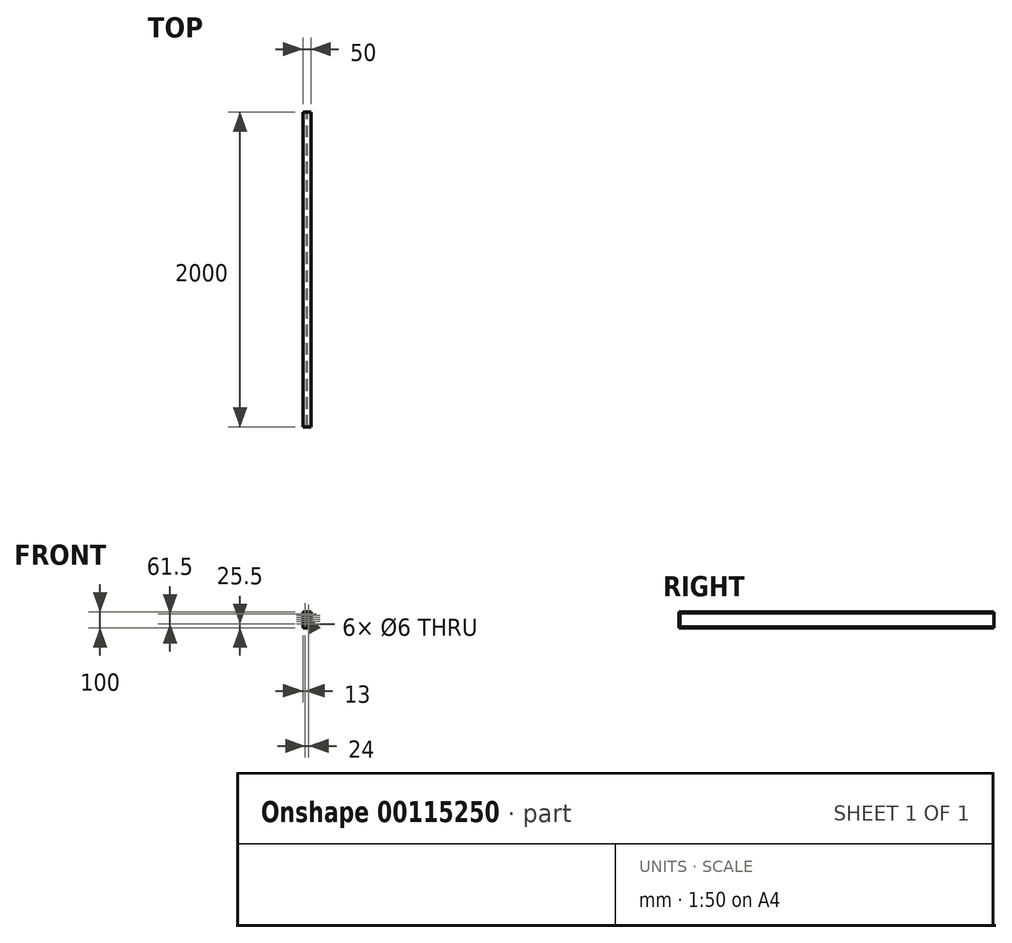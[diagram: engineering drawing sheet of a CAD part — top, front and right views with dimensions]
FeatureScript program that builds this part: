
annotation { "Feature Type Name" : "Feature", "Feature Type Description" : "" }
export const myFeature = defineFeature(function(context is Context, id is Id, definition is map)
    precondition{}
    {
        {
            var Q0;
            Q0=qCreatedBy(makeId("Front.planeOp"),FACE);
            var sketch = newSketch(context, id + "F0", { "sketchPlane" : qUnion([Q0])});
            skLineSegment(sketch, "E0.bottom", {"start": v(25, 50) * mm, "end": v(-25, 50) * mm});
            skLineSegment(sketch, "E0.top", {"start": v(25, -50) * mm, "end": v(-25, -50) * mm});
            skLineSegment(sketch, "E0.left", {"start": v(25, 50) * mm, "end": v(25, 44) * mm});
            skLineSegment(sketch, "E0.right", {"start": v(-25, 50) * mm, "end": v(-25, 44) * mm});
            skLineSegment(sketch, "E1.bottom", {"start": v(-25, 44) * mm, "end": v(-2.5, 44) * mm});
            skLineSegment(sketch, "E1.top", {"start": v(-25, -44) * mm, "end": v(-2.5, -44) * mm});
            skLineSegment(sketch, "E1.right", {"start": v(-2.5, 44) * mm, "end": v(-2.5, -44) * mm});
            skLineSegment(sketch, "E2.bottom", {"start": v(25, 44) * mm, "end": v(2.5, 44) * mm});
            skLineSegment(sketch, "E2.top", {"start": v(25, -44) * mm, "end": v(2.5, -44) * mm});
            skLineSegment(sketch, "E2.right", {"start": v(2.5, 44) * mm, "end": v(2.5, -44) * mm});
            skPoint(sketch, "E3.orphan", {"position": v(0, 50) * mm});
            skPoint(sketch, "E4.orphan", {"position": v(0, -50) * mm});
            skLineSegment(sketch, "E5.trimOffspring", {"start": v(-25, -44) * mm, "end": v(-25, -50) * mm});
            skLineSegment(sketch, "E6.trimOffspring", {"start": v(25, -44) * mm, "end": v(25, -50) * mm});
            skLineSegment(sketch, "E7", {"start": v(0, 50) * mm, "end": v(0, -50) * mm, "construction": true});
            skSolve(sketch);
        }
        {
            var Q0;
            Q0=makeQuery(id+"F0.imprint","IMPRINT",FACE,{"disambiguationData":[TD([[makeQuery(id+"F0.imprint","IMPRINT",EDGE,{"derivedFrom":sQuery(id+"F0.wireOp",EDGE,"E0.bottom")}),1.0]])]});
            extrude(context, id + "F1", {"entities" : qUnion([Q0]), "depth" : 2000 * mm});
        }
        {
            var Q0;
            Q0=makeQuery(id+"F1.opExtrude","CAP_FACE",FACE,{"disambiguationData":[OSD([sQuery(id+"F0.wireOp",EDGE,"E0.bottom"),sQuery(id+"F0.wireOp",EDGE,"E0.top"),sQuery(id+"F0.wireOp",EDGE,"E0.left"),sQuery(id+"F0.wireOp",EDGE,"E0.right"),sQuery(id+"F0.wireOp",EDGE,"E1.bottom"),sQuery(id+"F0.wireOp",EDGE,"E1.top"),sQuery(id+"F0.wireOp",EDGE,"E1.right"),sQuery(id+"F0.wireOp",EDGE,"E2.bottom"),sQuery(id+"F0.wireOp",EDGE,"E2.top"),sQuery(id+"F0.wireOp",EDGE,"E2.right"),sQuery(id+"F0.wireOp",EDGE,"E5.trimOffspring"),sQuery(id+"F0.wireOp",EDGE,"E6.trimOffspring")])],"isStart":false});
            var sketch = newSketch(context, id + "F2", { "sketchPlane" : qUnion([Q0])});
            skLineSegment(sketch, "E8.bottom", {"start": v(-2.5, 44) * mm, "end": v(-25, 44) * mm});
            skLineSegment(sketch, "E8.top", {"start": v(-2.5, -44) * mm, "end": v(-25, -44) * mm});
            skLineSegment(sketch, "E8.left", {"start": v(-2.5, 44) * mm, "end": v(-2.5, -44) * mm});
            skLineSegment(sketch, "E8.right", {"start": v(-25, 44) * mm, "end": v(-25, -44) * mm});
            skSolve(sketch);
        }
        {
            var Q0;
            Q0=makeQuery(id+"F2.imprint","IMPRINT",FACE,{"disambiguationData":[TD([[makeQuery(id+"F2.imprint","IMPRINT",EDGE,{"derivedFrom":sQuery(id+"F2.wireOp",EDGE,"E8.bottom")}),-1.0]])]});
            extrude(context, id + "F3", {"entities" : qUnion([Q0]), "oppositeDirection" : true, "depth" : 6 * mm});
        }
        {
            var Q0;
            Q0=makeQuery(id+"F1.opExtrude","CAP_FACE",FACE,{"disambiguationData":[OSD([sQuery(id+"F0.wireOp",EDGE,"E0.bottom"),sQuery(id+"F0.wireOp",EDGE,"E0.top"),sQuery(id+"F0.wireOp",EDGE,"E0.left"),sQuery(id+"F0.wireOp",EDGE,"E0.right"),sQuery(id+"F0.wireOp",EDGE,"E1.bottom"),sQuery(id+"F0.wireOp",EDGE,"E1.top"),sQuery(id+"F0.wireOp",EDGE,"E1.right"),sQuery(id+"F0.wireOp",EDGE,"E2.bottom"),sQuery(id+"F0.wireOp",EDGE,"E2.top"),sQuery(id+"F0.wireOp",EDGE,"E2.right"),sQuery(id+"F0.wireOp",EDGE,"E5.trimOffspring"),sQuery(id+"F0.wireOp",EDGE,"E6.trimOffspring")])],"isStart":false});
            var sketch = newSketch(context, id + "F4", { "sketchPlane" : qUnion([Q0])});
            skLineSegment(sketch, "E9.bottom", {"start": v(2.5, 44) * mm, "end": v(25, 44) * mm});
            skLineSegment(sketch, "E9.top", {"start": v(2.5, -44) * mm, "end": v(25, -44) * mm});
            skLineSegment(sketch, "E9.left", {"start": v(2.5, 44) * mm, "end": v(2.5, -44) * mm});
            skLineSegment(sketch, "E9.right", {"start": v(25, 44) * mm, "end": v(25, -44) * mm});
            skSolve(sketch);
        }
        {
            var Q0;
            Q0=makeQuery(id+"F4.imprint","IMPRINT",FACE,{"disambiguationData":[TD([[makeQuery(id+"F4.imprint","IMPRINT",EDGE,{"derivedFrom":sQuery(id+"F4.wireOp",EDGE,"E9.bottom")}),1.0]])]});
            extrude(context, id + "F5", {"entities" : qUnion([Q0]), "oppositeDirection" : true, "depth" : 6 * mm});
        }
        {
            var Q0;
            Q0=makeQuery(id+"F5.opExtrude","CAP_FACE",FACE,{"disambiguationData":[OSD([sQuery(id+"F4.wireOp",EDGE,"E9.bottom"),sQuery(id+"F4.wireOp",EDGE,"E9.top"),sQuery(id+"F4.wireOp",EDGE,"E9.left"),sQuery(id+"F4.wireOp",EDGE,"E9.right")])],"isStart":false});
            var sketch = newSketch(context, id + "F6", { "sketchPlane" : qUnion([Q0])});
            skPoint(sketch, "E10", {"position": v(-12, 27.5) * mm});
            skPoint(sketch, "E11", {"position": v(-12, 14.5) * mm});
            skPoint(sketch, "E12", {"position": v(-12, 1.5) * mm});
            skPoint(sketch, "E13", {"position": v(-12, -11.5) * mm});
            skPoint(sketch, "E14", {"position": v(-12, -24.5) * mm});
            skSolve(sketch);
        }
        {
            var Q0;
            Q0=sQuery(id+"F6.wireOp",VERTEX,"E10");
            var Q1;
            Q1=sQuery(id+"F6.wireOp",VERTEX,"E11");
            var Q2;
            Q2=sQuery(id+"F6.wireOp",VERTEX,"E12");
            var Q3;
            Q3=sQuery(id+"F6.wireOp",VERTEX,"E13");
            var Q4;
            Q4=sQuery(id+"F6.wireOp",VERTEX,"E14");
            var Q5;
            Q5=makeQuery(id+"F5.opExtrude","SWEPT_BODY",BODY,{"disambiguationData":[OSD([sQuery(id+"F4.wireOp",EDGE,"E9.bottom"),sQuery(id+"F4.wireOp",EDGE,"E9.top"),sQuery(id+"F4.wireOp",EDGE,"E9.left"),sQuery(id+"F4.wireOp",EDGE,"E9.right")])]});
            hole(context, id + "F7", {"style" : HoleStyle.SIMPLE, "endStyle" : HoleEndStyle.THROUGH, "holeDiameter" : 6 * mm, "locations" : qUnion([Q0, Q1, Q2, Q3, Q4]), "scope" : qUnion([Q5]), "isTappedThrough" : true});
        }
        {
            var Q0;
            Q0=makeQuery(id+"F3.opExtrude","CAP_FACE",FACE,{"disambiguationData":[OSD([sQuery(id+"F2.wireOp",EDGE,"E8.bottom"),sQuery(id+"F2.wireOp",EDGE,"E8.top"),sQuery(id+"F2.wireOp",EDGE,"E8.left"),sQuery(id+"F2.wireOp",EDGE,"E8.right")])],"isStart":false});
            var sketch = newSketch(context, id + "F8", { "sketchPlane" : qUnion([Q0])});
            skPoint(sketch, "E15", {"position": v(12, 37) * mm});
            skSolve(sketch);
        }
        {
            var Q0;
            Q0=sQuery(id+"F8.wireOp",VERTEX,"E15");
            var Q1;
            Q1=makeQuery(id+"F3.opExtrude","SWEPT_BODY",BODY,{"disambiguationData":[OSD([sQuery(id+"F2.wireOp",EDGE,"E8.bottom"),sQuery(id+"F2.wireOp",EDGE,"E8.top"),sQuery(id+"F2.wireOp",EDGE,"E8.left"),sQuery(id+"F2.wireOp",EDGE,"E8.right")])]});
            hole(context, id + "F9", {"style" : HoleStyle.SIMPLE, "endStyle" : HoleEndStyle.THROUGH, "holeDiameter" : 6 * mm, "locations" : qUnion([Q0]), "scope" : qUnion([Q1]), "isTappedThrough" : true});
        }
    });
